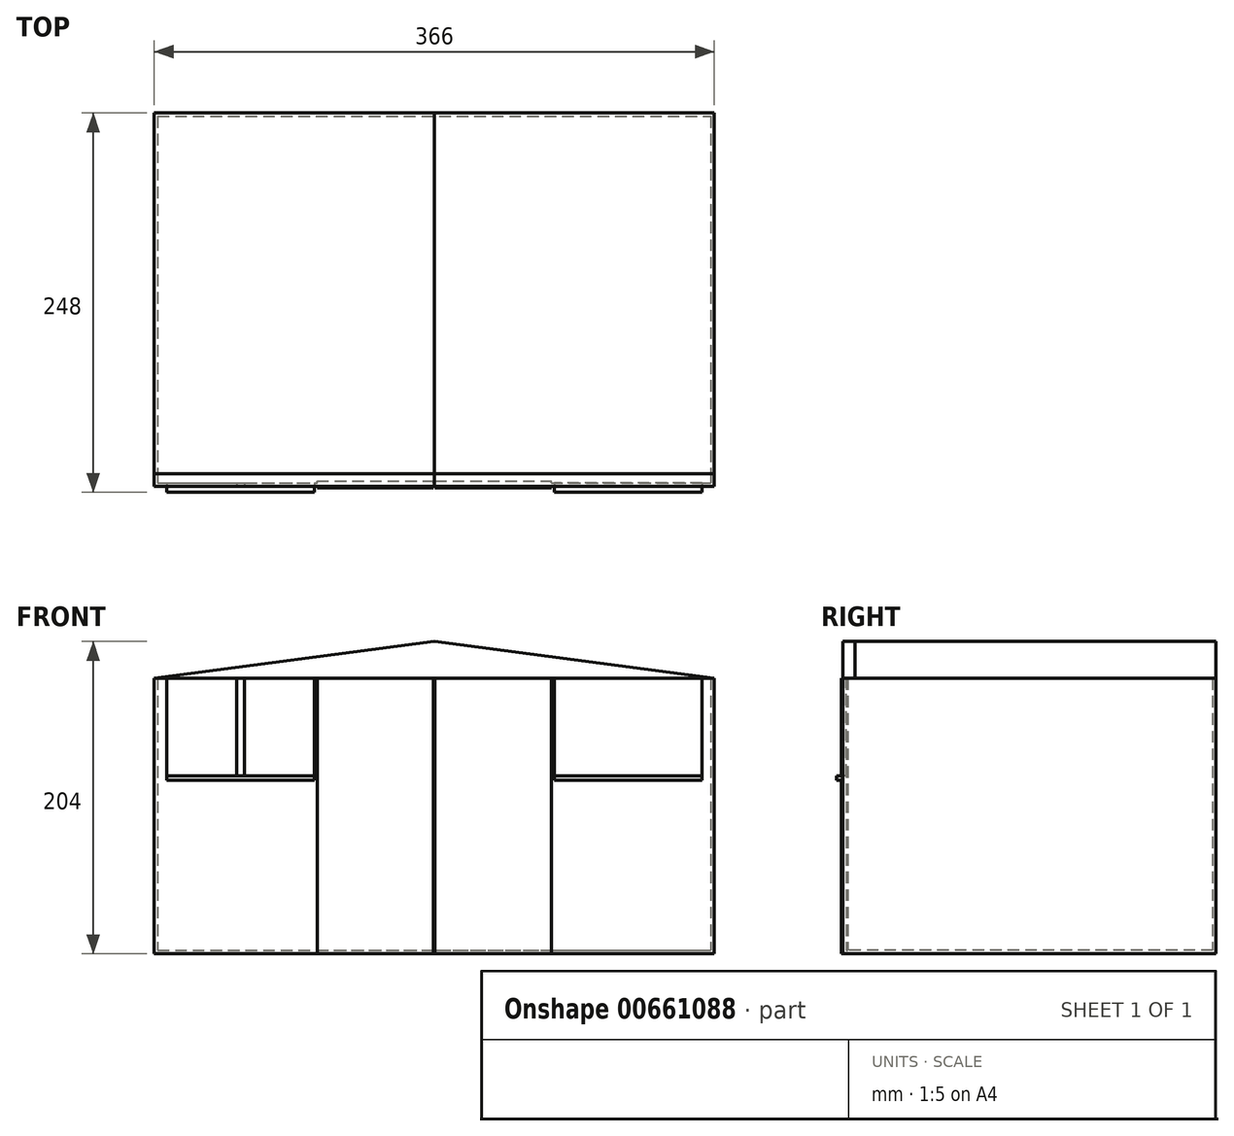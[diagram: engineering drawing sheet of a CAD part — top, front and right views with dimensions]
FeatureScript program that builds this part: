
annotation { "Feature Type Name" : "Feature", "Feature Type Description" : "" }
export const myFeature = defineFeature(function(context is Context, id is Id, definition is map)
    precondition{}
    {
        {
            var Q0;
            Q0=qCreatedBy(makeId("Top.planeOp"),FACE);
            var sketch = newSketch(context, id + "F0", { "sketchPlane" : qUnion([Q0])});
            skLineSegment(sketch, "E0.bottom", {"start": v(0, 0) * mm, "end": v(366, 0) * mm});
            skLineSegment(sketch, "E0.top", {"start": v(0, -244) * mm, "end": v(366, -244) * mm});
            skLineSegment(sketch, "E0.left", {"start": v(0, 0) * mm, "end": v(0, -244) * mm});
            skLineSegment(sketch, "E0.right", {"start": v(366, 0) * mm, "end": v(366, -244) * mm});
            skLineSegment(sketch, "E1.bottom", {"start": v(2.2, -2.2) * mm, "end": v(363.8, -2.2) * mm});
            skLineSegment(sketch, "E1.top", {"start": v(2.2, -241.8) * mm, "end": v(363.8, -241.8) * mm});
            skLineSegment(sketch, "E1.left", {"start": v(2.2, -2.2) * mm, "end": v(2.2, -241.8) * mm});
            skLineSegment(sketch, "E1.right", {"start": v(363.8, -2.2) * mm, "end": v(363.8, -241.8) * mm});
            skLineSegment(sketch, "E2.top", {"start": v(0, -304) * mm, "end": v(366, -304) * mm});
            skLineSegment(sketch, "E2.left", {"start": v(0, -244) * mm, "end": v(0, -304) * mm});
            skLineSegment(sketch, "E2.right", {"start": v(366, -244) * mm, "end": v(366, -304) * mm});
            skSolve(sketch);
        }
        {
            var Q0;
            Q0=makeQuery(id+"F0.imprint","IMPRINT",FACE,{"disambiguationData":[TD([[makeQuery(id+"F0.imprint","IMPRINT",EDGE,{"derivedFrom":sQuery(id+"F0.wireOp",EDGE,"E0.bottom")}),-1.0]])]});
            extrude(context, id + "F1", {"entities" : qUnion([Q0]), "depth" : 180 * mm, "offsetDistance" : 25 * mm});
        }
        {
            var Q0;
            Q0=makeQuery(id+"F0.imprint","IMPRINT",FACE,{"disambiguationData":[TD([[makeQuery(id+"F0.imprint","IMPRINT",EDGE,{"derivedFrom":sQuery(id+"F0.wireOp",EDGE,"E1.bottom")}),-1.0]])]});
            extrude(context, id + "F2", {"entities" : qUnion([Q0]), "operationType" : NewBodyOperationType.ADD, "depth" : 2.2 * mm, "offsetDistance" : 25 * mm});
        }
        {
            var Q0;
            Q0=makeQuery(id+"F1.opExtrude","SWEPT_FACE",FACE,{"disambiguationData":[OSD([sQuery(id+"F0.wireOp",EDGE,"E0.top")])]});
            var sketch = newSketch(context, id + "F3", { "sketchPlane" : qUnion([Q0])});
            skLineSegment(sketch, "E3.bottom", {"start": v(106.5, 180) * mm, "end": v(182.5, 180) * mm});
            skLineSegment(sketch, "E3.top", {"start": v(106.5, 0) * mm, "end": v(182.5, 0) * mm});
            skLineSegment(sketch, "E3.left", {"start": v(106.5, 180) * mm, "end": v(106.5, 0) * mm});
            skLineSegment(sketch, "E3.right", {"start": v(182.5, 180) * mm, "end": v(182.5, 0) * mm});
            skLineSegment(sketch, "E4.bottom", {"start": v(183.5, 180) * mm, "end": v(259.5, 180) * mm});
            skLineSegment(sketch, "E4.top", {"start": v(183.5, 0) * mm, "end": v(259.5, 0) * mm});
            skLineSegment(sketch, "E4.left", {"start": v(183.5, 180) * mm, "end": v(183.5, 0) * mm});
            skLineSegment(sketch, "E4.right", {"start": v(259.5, 180) * mm, "end": v(259.5, 0) * mm});
            skPoint(sketch, "E5", {"position": v(183, 2.2) * mm});
            skPoint(sketch, "E6", {"position": v(182.5, 0) * mm});
            skPoint(sketch, "E7", {"position": v(183.5, 0) * mm});
            skLineSegment(sketch, "E8.bottom", {"start": v(104.5, 180) * mm, "end": v(8, 180) * mm});
            skLineSegment(sketch, "E8.top", {"start": v(104.5, 116.29) * mm, "end": v(8, 116.29) * mm});
            skLineSegment(sketch, "E8.left", {"start": v(104.5, 180) * mm, "end": v(104.5, 116.29) * mm});
            skLineSegment(sketch, "E8.right", {"start": v(8, 180) * mm, "end": v(8, 116.29) * mm});
            skLineSegment(sketch, "E9.bottom", {"start": v(261.5, 180) * mm, "end": v(358, 180) * mm});
            skLineSegment(sketch, "E9.top", {"start": v(261.5, 116.29) * mm, "end": v(358, 116.29) * mm});
            skLineSegment(sketch, "E9.left", {"start": v(261.5, 180) * mm, "end": v(261.5, 116.29) * mm});
            skLineSegment(sketch, "E9.right", {"start": v(358, 180) * mm, "end": v(358, 116.29) * mm});
            skPoint(sketch, "E10", {"position": v(56.25, 180) * mm});
            skPoint(sketch, "E11", {"position": v(56.25, 116.29) * mm});
            skPoint(sketch, "E12", {"position": v(8, 148.14) * mm});
            skPoint(sketch, "E13", {"position": v(309.75, 180) * mm});
            skLineSegment(sketch, "E14.bottom", {"start": v(8, 116.29) * mm, "end": v(104.5, 116.29) * mm});
            skLineSegment(sketch, "E14.top", {"start": v(8, 113.29) * mm, "end": v(104.5, 113.29) * mm});
            skLineSegment(sketch, "E14.left", {"start": v(8, 116.29) * mm, "end": v(8, 113.29) * mm});
            skLineSegment(sketch, "E14.right", {"start": v(104.5, 116.29) * mm, "end": v(104.5, 113.29) * mm});
            skLineSegment(sketch, "E15.top", {"start": v(261.5, 113.29) * mm, "end": v(358, 113.29) * mm});
            skLineSegment(sketch, "E15.left", {"start": v(261.5, 116.29) * mm, "end": v(261.5, 113.29) * mm});
            skLineSegment(sketch, "E15.right", {"start": v(358, 116.29) * mm, "end": v(358, 113.29) * mm});
            skLineSegment(sketch, "E16", {"start": v(0, 180) * mm, "end": v(183, 204) * mm});
            skLineSegment(sketch, "E17", {"start": v(183, 204) * mm, "end": v(366, 180) * mm});
            skLineSegment(sketch, "E18.bottom", {"start": v(53.75, 180) * mm, "end": v(58.75, 180) * mm});
            skLineSegment(sketch, "E18.top", {"start": v(53.75, 116.29) * mm, "end": v(58.75, 116.29) * mm});
            skLineSegment(sketch, "E18.left", {"start": v(53.75, 180) * mm, "end": v(53.75, 116.29) * mm});
            skLineSegment(sketch, "E18.right", {"start": v(58.75, 180) * mm, "end": v(58.75, 116.29) * mm});
            skLineSegment(sketch, "E19.bottom", {"start": v(307.25, 180) * mm, "end": v(312.25, 180) * mm});
            skLineSegment(sketch, "E19.top", {"start": v(307.25, 116.29) * mm, "end": v(312.25, 116.29) * mm});
            skLineSegment(sketch, "E19.left", {"start": v(307.25, 180) * mm, "end": v(307.25, 116.29) * mm});
            skLineSegment(sketch, "E19.right", {"start": v(312.25, 180) * mm, "end": v(312.25, 116.29) * mm});
            skSolve(sketch);
        }
        {
            var Q0;
            Q0=makeQuery(id+"F3.imprint","IMPRINT",FACE,{"disambiguationData":[TD([[makeQuery(id+"F3.imprint","IMPRINT",EDGE,{"derivedFrom":sQuery(id+"F3.wireOp",EDGE,"E3.bottom")}),-1.0]])]});
            var Q1;
            Q1=makeQuery(id+"F3.imprint","IMPRINT",FACE,{"disambiguationData":[TD([[makeQuery(id+"F3.imprint","IMPRINT",EDGE,{"derivedFrom":sQuery(id+"F3.wireOp",EDGE,"E4.bottom")}),-1.0]])]});
            var Q2;
            Q2=makeQuery(id+"F3.imprint","IMPRINT",FACE,{"disambiguationData":[TD([[makeQuery(id+"F3.imprint","IMPRINT",EDGE,{"derivedFrom":sQuery(id+"F3.wireOp",EDGE,"E18.bottom")}),-1.0]])]});
            var Q3;
            Q3=makeQuery(id+"F3.imprint","IMPRINT",FACE,{"disambiguationData":[TD([[makeQuery(id+"F3.imprint","IMPRINT",EDGE,{"derivedFrom":sQuery(id+"F3.wireOp",EDGE,"E19.bottom")}),-1.0]])]});
            extrude(context, id + "F4", {"entities" : qUnion([Q0, Q1, Q2, Q3]), "operationType" : NewBodyOperationType.ADD, "depth" : 1 * mm, "offsetDistance" : 25 * mm, "hasSecondDirection" : true, "secondDirectionOppositeDirection" : true, "secondDirectionDepth" : 3.3 * mm});
        }
        {
            var Q0;
            Q0=makeQuery(id+"F3.imprint","IMPRINT",FACE,{"disambiguationData":[TD([[makeQuery(id+"F3.imprint","IMPRINT",EDGE,{"derivedFrom":sQuery(id+"F3.wireOp",EDGE,"E8.bottom")}),1.0]])]});
            var Q1;
            Q1=makeQuery(id+"F3.imprint","IMPRINT",FACE,{"disambiguationData":[TD([[makeQuery(id+"F3.imprint","IMPRINT",EDGE,{"derivedFrom":sQuery(id+"F3.wireOp",EDGE,"E9.bottom")}),-1.0]])]});
            var Q2;
            {var subQ0=sQuery(id+"F3.wireOp",EDGE,"E9.left");var subQ1=sQuery(id+"F3.wireOp",EDGE,"E9.top");var subQ2=makeQuery(id+"F3.imprint","INTERSECT",VERTEX,{"derivedFrom":[subQ1,subQ0]});Q2=makeQuery(id+"F3.imprint","IMPRINT",FACE,{"disambiguationData":[TD([[makeQuery(id+"F3.imprint","IMPRINT",EDGE,{"disambiguationData":[TD([[subQ2,-1.0]])],"derivedFrom":subQ1}),1.0]])]});}
            var Q3;
            {var subQ7=sQuery(id+"F3.wireOp",EDGE,"YfnkvgQr-QRok-V14t-g57v-lyYDbdyxjaZ6.top");Q3=makeQuery(id+"F3.imprint","IMPRINT",FACE,{"disambiguationData":[TD([[makeQuery(id+"F3.imprint","IMPRINT",EDGE,{"derivedFrom":subQ7}),1.0]])]});}
            var Q4;
            {var subQ0=sQuery(id+"F3.wireOp",EDGE,"YfnkvgQr-QRok-V14t-g57v-lyYDbdyxjaZ6.bottom");Q4=makeQuery(id+"F3.imprint","IMPRINT",FACE,{"disambiguationData":[TD([[makeQuery(id+"F3.imprint","IMPRINT",EDGE,{"derivedFrom":subQ0}),-1.0]])]});}
            var Q5;
            {var subQ0=sQuery(id+"F3.wireOp",EDGE,"E8.left");var subQ1=sQuery(id+"F3.wireOp",EDGE,"E8.top");var subQ2=makeQuery(id+"F3.imprint","INTERSECT",VERTEX,{"derivedFrom":[subQ1,subQ0]});Q5=makeQuery(id+"F3.imprint","IMPRINT",FACE,{"disambiguationData":[TD([[makeQuery(id+"F3.imprint","IMPRINT",EDGE,{"disambiguationData":[TD([[subQ2,-1.0]])],"derivedFrom":subQ1}),-1.0]])]});}
            var Q6;
            {var subQ0=sQuery(id+"F3.wireOp",EDGE,"E8.right");var subQ1=sQuery(id+"F3.wireOp",EDGE,"E8.top");var subQ2=makeQuery(id+"F3.imprint","INTERSECT",VERTEX,{"derivedFrom":[subQ1,subQ0]});Q6=makeQuery(id+"F3.imprint","IMPRINT",FACE,{"disambiguationData":[TD([[makeQuery(id+"F3.imprint","IMPRINT",EDGE,{"disambiguationData":[TD([[subQ2,1.0]])],"derivedFrom":subQ1}),-1.0]])]});}
            var Q7;
            {var subQ0=sQuery(id+"F3.wireOp",EDGE,"E14.bottom");var subQ5=sQuery(id+"F3.wireOp",EDGE,"sOry4WVp-PIxf-8NyE-KQ36-WmRoLQExKCCO.left");var subQ6=makeQuery(id+"F3.imprint","INTERSECT",VERTEX,{"derivedFrom":[subQ5,subQ0]});Q7=makeQuery(id+"F3.imprint","IMPRINT",FACE,{"disambiguationData":[TD([[makeQuery(id+"F3.imprint","IMPRINT",EDGE,{"disambiguationData":[TD([[subQ6,1.0]])],"derivedFrom":subQ5}),-1.0]])]});}
            var Q8;
            {var subQ0=sQuery(id+"F3.wireOp",EDGE,"E14.bottom");var subQ5=sQuery(id+"F3.wireOp",EDGE,"sOry4WVp-PIxf-8NyE-KQ36-WmRoLQExKCCO.right");var subQ6=makeQuery(id+"F3.imprint","INTERSECT",VERTEX,{"derivedFrom":[subQ5,subQ0]});Q8=makeQuery(id+"F3.imprint","IMPRINT",FACE,{"disambiguationData":[TD([[makeQuery(id+"F3.imprint","IMPRINT",EDGE,{"disambiguationData":[TD([[subQ6,1.0]])],"derivedFrom":subQ5}),1.0]])]});}
            var Q9;
            {var subQ0=sQuery(id+"F3.wireOp",EDGE,"E9.top");var subQ5=sQuery(id+"F3.wireOp",EDGE,"OYBSw6cz-BSUv-Zrt5-bxVA-wndxCvquLag2.left");var subQ7=makeQuery(id+"F3.imprint","INTERSECT",VERTEX,{"derivedFrom":[subQ5,subQ0]});Q9=makeQuery(id+"F3.imprint","IMPRINT",FACE,{"disambiguationData":[TD([[makeQuery(id+"F3.imprint","IMPRINT",EDGE,{"disambiguationData":[TD([[subQ7,1.0]])],"derivedFrom":subQ5}),-1.0]])]});}
            var Q10;
            {var subQ0=sQuery(id+"F3.wireOp",EDGE,"E9.top");var subQ3=makeQuery(id+"F3.imprint","IMPRINT",VERTEX,{"disambiguationData":[OD(1.0)],"derivedFrom":subQ0});Q10=makeQuery(id+"F3.imprint","IMPRINT",FACE,{"disambiguationData":[TD([[makeQuery(id+"F3.imprint","IMPRINT",EDGE,{"disambiguationData":[TD([[subQ3,1.0]])],"derivedFrom":subQ0}),1.0]])]});}
            extrude(context, id + "F5", {"entities" : qUnion([Q0, Q1, Q2, Q3, Q4, Q5, Q6, Q7, Q8, Q9, Q10]), "operationType" : NewBodyOperationType.REMOVE, "oppositeDirection" : true, "depth" : 25 * mm, "offsetDistance" : 25 * mm});
        }
        {
            var Q0;
            {var subQ10=sQuery(id+"F3.wireOp",EDGE,"E3.bottom");Q0=makeQuery(id+"F3.imprint","IMPRINT",FACE,{"disambiguationData":[TD([[makeQuery(id+"F3.imprint","IMPRINT",EDGE,{"derivedFrom":subQ10}),1.0]])]});}
            extrude(context, id + "F6", {"entities" : qUnion([Q0]), "operationType" : NewBodyOperationType.ADD, "oppositeDirection" : true, "depth" : 8 * mm, "offsetDistance" : 25 * mm});
        }
        {
            var Q0;
            Q0=makeQuery(id+"F3.imprint","IMPRINT",FACE,{"disambiguationData":[TD([[makeQuery(id+"F3.imprint","IMPRINT",EDGE,{"derivedFrom":sQuery(id+"F3.wireOp",EDGE,"E15.top")}),1.0]])]});
            var Q1;
            Q1=makeQuery(id+"F3.imprint","IMPRINT",FACE,{"disambiguationData":[TD([[makeQuery(id+"F3.imprint","IMPRINT",EDGE,{"derivedFrom":sQuery(id+"F3.wireOp",EDGE,"E14.top")}),1.0]])]});
            extrude(context, id + "F7", {"entities" : qUnion([Q0, Q1]), "operationType" : NewBodyOperationType.ADD, "depth" : 4 * mm, "offsetDistance" : 25 * mm});
        }
        {
            var Q0;
            Q0=makeQuery(id+"F1.opExtrude","SWEPT_FACE",FACE,{"disambiguationData":[OSD([sQuery(id+"F0.wireOp",EDGE,"E0.bottom")])]});
            var sketch = newSketch(context, id + "F8", { "sketchPlane" : qUnion([Q0])});
            skLineSegment(sketch, "E20", {"start": v(-366, 180) * mm, "end": v(-183, 204) * mm});
            skPoint(sketch, "E20.endSnap0", {"position": v(-183, 180) * mm});
            skLineSegment(sketch, "E21", {"start": v(-183, 204) * mm, "end": v(0, 180) * mm});
            skSolve(sketch);
        }
        {
            var Q0;
            Q0=makeQuery(id+"F8.imprint","IMPRINT",FACE,{"disambiguationData":[TD([[makeQuery(id+"F8.imprint","IMPRINT",EDGE,{"derivedFrom":sQuery(id+"F8.wireOp",EDGE,"E20")}),-1.0]])]});
            extrude(context, id + "F9", {"entities" : qUnion([Q0]), "oppositeDirection" : true, "depth" : 244 * mm, "offsetDistance" : 25 * mm});
        }
    });
